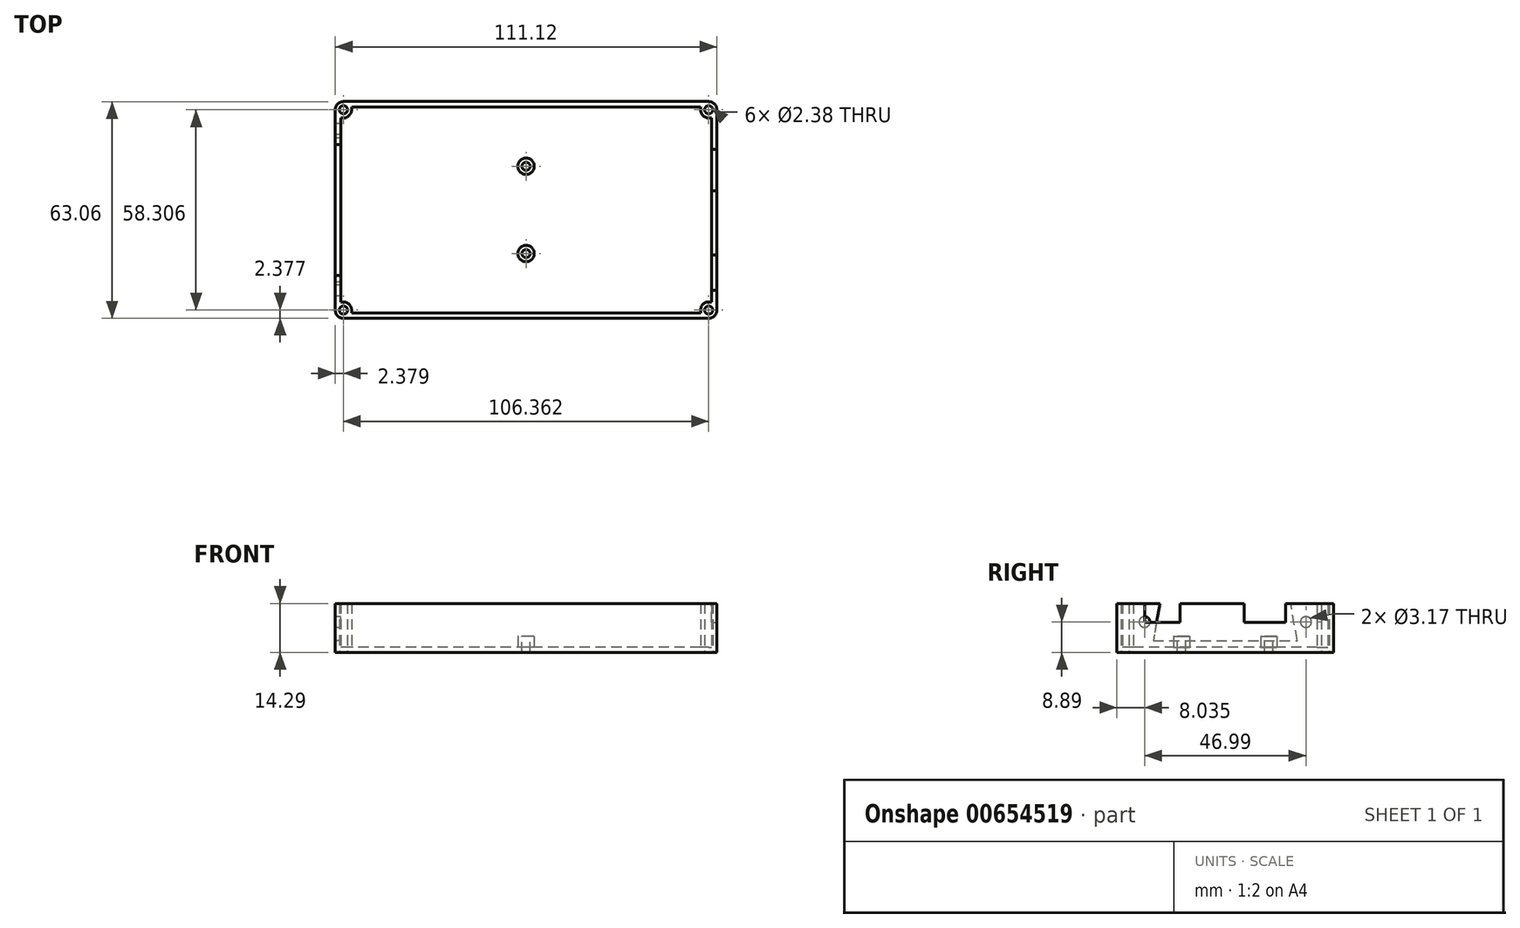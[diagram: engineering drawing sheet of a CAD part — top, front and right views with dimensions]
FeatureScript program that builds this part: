
annotation { "Feature Type Name" : "Feature", "Feature Type Description" : "" }
export const myFeature = defineFeature(function(context is Context, id is Id, definition is map)
    precondition{}
    {
        {
            var Q0;
            Q0=qCreatedBy(makeId("Top.planeOp"),FACE);
            var sketch = newSketch(context, id + "F0", { "sketchPlane" : qUnion([Q0])});
            skLineSegment(sketch, "E0.bottom", {"start": v(50.8, 26.77) * mm, "end": v(-50.8, 26.77) * mm});
            skLineSegment(sketch, "E0.top", {"start": v(50.8, -26.77) * mm, "end": v(-50.8, -26.77) * mm});
            skLineSegment(sketch, "E0.left", {"start": v(50.8, 26.77) * mm, "end": v(50.8, -26.77) * mm});
            skLineSegment(sketch, "E0.right", {"start": v(-50.8, 26.77) * mm, "end": v(-50.8, -26.77) * mm});
            skPoint(sketch, "E0.middle", {"position": v(0, 0) * mm});
            skSolve(sketch);
        }
        {
            var Q0;
            Q0=qCreatedBy(makeId("Top.planeOp"),FACE);
            var sketch = newSketch(context, id + "F1", { "sketchPlane" : qUnion([Q0])});
            skLineSegment(sketch, "E1.bottom", {"start": v(55.56, 31.53) * mm, "end": v(-55.56, 31.53) * mm});
            skLineSegment(sketch, "E1.top", {"start": v(55.56, -31.53) * mm, "end": v(-55.56, -31.53) * mm});
            skLineSegment(sketch, "E1.left", {"start": v(55.56, 31.53) * mm, "end": v(55.56, -31.53) * mm});
            skLineSegment(sketch, "E1.right", {"start": v(-55.56, 31.53) * mm, "end": v(-55.56, -31.53) * mm});
            skPoint(sketch, "E1.middle", {"position": v(0, 0) * mm});
            skLineSegment(sketch, "E2.bottom", {"start": v(53.97, 29.95) * mm, "end": v(-53.98, 29.95) * mm, "construction": true});
            skLineSegment(sketch, "E2.top", {"start": v(53.98, -29.95) * mm, "end": v(-53.97, -29.95) * mm, "construction": true});
            skLineSegment(sketch, "E2.left", {"start": v(53.97, 29.95) * mm, "end": v(53.98, -29.95) * mm, "construction": true});
            skLineSegment(sketch, "E2.right", {"start": v(-53.98, 29.95) * mm, "end": v(-53.97, -29.95) * mm, "construction": true});
            skSolve(sketch);
        }
        {
            var Q0;
            Q0=makeQuery(id+"F1.imprint","IMPRINT",FACE,{"disambiguationData":[TD([[makeQuery(id+"F1.imprint","IMPRINT",EDGE,{"derivedFrom":sQuery(id+"F1.wireOp",EDGE,"E1.bottom")}),1.0]])]});
            extrude(context, id + "F2", {"entities" : qUnion([Q0]), "depth" : 1.59 * mm, "offsetDistance" : 25.4 * mm});
        }
        {
            var Q0;
            Q0=makeQuery(id+"F2.opExtrude","CAP_FACE",FACE,{"disambiguationData":[OSD([sQuery(id+"F1.wireOp",EDGE,"E1.bottom"),sQuery(id+"F1.wireOp",EDGE,"E1.top"),sQuery(id+"F1.wireOp",EDGE,"E1.left"),sQuery(id+"F1.wireOp",EDGE,"E1.right")])],"isStart":false});
            var sketch = newSketch(context, id + "F3", { "sketchPlane" : qUnion([Q0])});
            skLineSegment(sketch, "E3.bottom", {"start": v(55.56, 31.53) * mm, "end": v(-55.56, 31.53) * mm});
            skLineSegment(sketch, "E3.top", {"start": v(55.56, -31.53) * mm, "end": v(-55.56, -31.53) * mm});
            skLineSegment(sketch, "E3.left", {"start": v(55.56, 31.53) * mm, "end": v(55.56, -31.53) * mm});
            skLineSegment(sketch, "E3.right", {"start": v(-55.56, 31.53) * mm, "end": v(-55.56, -31.53) * mm});
            skPoint(sketch, "E3.middle", {"position": v(0, 0) * mm});
            skLineSegment(sketch, "E4.left", {"start": v(53.97, 26.77) * mm, "end": v(53.97, -26.77) * mm});
            skLineSegment(sketch, "E4.right", {"start": v(-53.97, 26.77) * mm, "end": v(-53.97, -26.77) * mm});
            skArc(sketch, "E5", {"start": v(-53.18, 26.77) * mm, "mid": v(-51.5, 27.47) * mm, "end": v(-50.8, 29.15) * mm});
            skCircle(sketch, "E6", {"center": v(-53.18, 29.15) * mm, "radius": 1.2 * mm});
            skLineSegment(sketch, "E7", {"start": v(-50.8, 29.15) * mm, "end": v(-50.8, 29.95) * mm});
            skLineSegment(sketch, "E8", {"start": v(-53.18, 26.77) * mm, "end": v(-53.97, 26.77) * mm});
            skLineSegment(sketch, "E9", {"start": v(-55.56, 31.53) * mm, "end": v(-51.5, 27.47) * mm, "construction": true});
            skPoint(sketch, "E10", {"position": v(-53.53, 29.5) * mm});
            skPoint(sketch, "E11.orphan", {"position": v(-53.97, 37.1) * mm});
            skCircle(sketch, "E12.MirrorC", {"center": v(-53.18, -29.15) * mm, "radius": 1.2 * mm});
            skLineSegment(sketch, "E13.MirrorCS", {"start": v(-53.18, -26.77) * mm, "end": v(-53.97, -26.77) * mm});
            skArc(sketch, "E14.MirrorCS", {"start": v(-53.18, -26.77) * mm, "mid": v(-51.5, -27.47) * mm, "end": v(-50.8, -29.15) * mm});
            skLineSegment(sketch, "E15.MirrorCS", {"start": v(-50.8, -29.15) * mm, "end": v(-50.8, -29.95) * mm});
            skCircle(sketch, "E16.MirrorC", {"center": v(53.18, 29.15) * mm, "radius": 1.2 * mm});
            skLineSegment(sketch, "E17.MirrorCS", {"start": v(50.8, 29.15) * mm, "end": v(50.8, 29.95) * mm});
            skArc(sketch, "E18.MirrorCS", {"start": v(53.18, 26.77) * mm, "mid": v(51.5, 27.47) * mm, "end": v(50.8, 29.15) * mm});
            skLineSegment(sketch, "E19.MirrorCS", {"start": v(53.18, 26.77) * mm, "end": v(53.97, 26.77) * mm});
            skCircle(sketch, "E20.MirrorC", {"center": v(53.18, -29.15) * mm, "radius": 1.2 * mm});
            skLineSegment(sketch, "E21.MirrorCS", {"start": v(53.18, -26.77) * mm, "end": v(53.97, -26.77) * mm});
            skArc(sketch, "E22.MirrorCS", {"start": v(53.18, -26.77) * mm, "mid": v(51.5, -27.47) * mm, "end": v(50.8, -29.15) * mm});
            skLineSegment(sketch, "E23.MirrorCS", {"start": v(50.8, -29.15) * mm, "end": v(50.8, -29.95) * mm});
            skPoint(sketch, "E24.orphan", {"position": v(-53.97, -36.92) * mm});
            skLineSegment(sketch, "E25.trimOffspring", {"start": v(50.8, -29.95) * mm, "end": v(-50.8, -29.95) * mm});
            skPoint(sketch, "E26.orphan", {"position": v(53.97, -37.1) * mm});
            skLineSegment(sketch, "E27.trimOffspring", {"start": v(50.8, 29.95) * mm, "end": v(-50.8, 29.95) * mm});
            skPoint(sketch, "E28.orphan", {"position": v(53.97, 36.92) * mm});
            skSolve(sketch);
        }
        {
            var Q0;
            Q0=qSketchRegion(id+"F3",true);
            extrude(context, id + "F4", {"entities" : qUnion([Q0]), "operationType" : NewBodyOperationType.ADD, "depth" : 12.7 * mm, "offsetDistance" : 25.4 * mm});
        }
        {
            var Q0;
            Q0=makeQuery(id+"F4.boolean.opBoolean","MERGE",EDGE,{"derivedFrom":[makeQuery(id+"F2.opExtrude","SWEPT_EDGE",EDGE,{"disambiguationData":[OSD([sQuery(id+"F1.wireOp",EDGE,"E1.top"),sQuery(id+"F1.wireOp",EDGE,"E1.left")])]}),makeQuery(id+"F4.opExtrude","SWEPT_EDGE",EDGE,{"disambiguationData":[OSD([sQuery(id+"F3.wireOp",EDGE,"E3.top"),sQuery(id+"F3.wireOp",EDGE,"E3.left")])]})]});
            var Q1;
            Q1=makeQuery(id+"F4.boolean.opBoolean","MERGE",EDGE,{"derivedFrom":[makeQuery(id+"F2.opExtrude","SWEPT_EDGE",EDGE,{"disambiguationData":[OSD([sQuery(id+"F1.wireOp",EDGE,"E1.bottom"),sQuery(id+"F1.wireOp",EDGE,"E1.left")])]}),makeQuery(id+"F4.opExtrude","SWEPT_EDGE",EDGE,{"disambiguationData":[OSD([sQuery(id+"F3.wireOp",EDGE,"E3.bottom"),sQuery(id+"F3.wireOp",EDGE,"E3.left")])]})]});
            var Q2;
            Q2=makeQuery(id+"F4.boolean.opBoolean","MERGE",EDGE,{"derivedFrom":[makeQuery(id+"F2.opExtrude","SWEPT_EDGE",EDGE,{"disambiguationData":[OSD([sQuery(id+"F1.wireOp",EDGE,"E1.top"),sQuery(id+"F1.wireOp",EDGE,"E1.right")])]}),makeQuery(id+"F4.opExtrude","SWEPT_EDGE",EDGE,{"disambiguationData":[OSD([sQuery(id+"F3.wireOp",EDGE,"E3.top"),sQuery(id+"F3.wireOp",EDGE,"E3.right")])]})]});
            var Q3;
            Q3=makeQuery(id+"F4.boolean.opBoolean","MERGE",EDGE,{"derivedFrom":[makeQuery(id+"F2.opExtrude","SWEPT_EDGE",EDGE,{"disambiguationData":[OSD([sQuery(id+"F1.wireOp",EDGE,"E1.bottom"),sQuery(id+"F1.wireOp",EDGE,"E1.right")])]}),makeQuery(id+"F4.opExtrude","SWEPT_EDGE",EDGE,{"disambiguationData":[OSD([sQuery(id+"F3.wireOp",EDGE,"E3.bottom"),sQuery(id+"F3.wireOp",EDGE,"E3.right")])]})]});
            fillet(context, id + "F5", {"entities" : qUnion([Q0, Q1, Q2, Q3]), "radius" : 2.38 * mm, "tangentPropagation" : true, "allowEdgeOverflow" : false});
        }
        {
            var Q0;
            Q0=makeQuery(id+"F4.boolean.opBoolean","MERGE",FACE,{"derivedFrom":[makeQuery(id+"F2.opExtrude","SWEPT_FACE",FACE,{"disambiguationData":[OSD([sQuery(id+"F1.wireOp",EDGE,"E1.left")])]}),makeQuery(id+"F4.opExtrude","SWEPT_FACE",FACE,{"disambiguationData":[OSD([sQuery(id+"F3.wireOp",EDGE,"E3.left")])]})]});
            var sketch = newSketch(context, id + "F6", { "sketchPlane" : qUnion([Q0])});
            skLineSegment(sketch, "E29.bottom", {"start": v(-17.59, 14.29) * mm, "end": v(-13.14, 14.29) * mm});
            skLineSegment(sketch, "E29.top", {"start": v(-17.59, 8.76) * mm, "end": v(-13.14, 8.76) * mm});
            skLineSegment(sketch, "E30.top", {"start": v(13.14, 8.76) * mm, "end": v(17.59, 8.76) * mm});
            skPoint(sketch, "E31", {"position": v(-11.56, 8.76) * mm});
            skPoint(sketch, "E32", {"position": v(18.29, 8.76) * mm});
            skLineSegment(sketch, "E33.MirrorCS", {"start": v(5.52, 14.29) * mm, "end": v(5.52, 8.76) * mm});
            skLineSegment(sketch, "E34.MirrorCS", {"start": v(13.14, 8.76) * mm, "end": v(5.52, 8.76) * mm});
            skLineSegment(sketch, "E35.MirrorCS", {"start": v(17.59, 14.29) * mm, "end": v(17.59, 8.76) * mm});
            skLineSegment(sketch, "E36.MirrorCS", {"start": v(-17.59, 14.29) * mm, "end": v(-23.43, 14.29) * mm});
            skLineSegment(sketch, "E37.MirrorCS", {"start": v(-17.59, 8.76) * mm, "end": v(-23.43, 8.76) * mm});
            skPoint(sketch, "E38.MirrorP", {"position": v(-18.29, 8.76) * mm});
            skLineSegment(sketch, "E39.MirrorCS", {"start": v(-13.14, 14.29) * mm, "end": v(-13.14, 8.76) * mm});
            skLineSegment(sketch, "E40.MirrorCS", {"start": v(-23.43, 14.29) * mm, "end": v(-23.43, 8.76) * mm});
            skLineSegment(sketch, "E41.MirrorCS", {"start": v(17.59, 14.29) * mm, "end": v(5.52, 14.29) * mm});
            skPoint(sketch, "E42.MirrorP", {"position": v(11.56, 8.76) * mm});
            skPoint(sketch, "E43.orphan", {"position": v(23.43, 14.29) * mm});
            skPoint(sketch, "E44.orphan", {"position": v(23.43, 8.76) * mm});
            skPoint(sketch, "E30.bottom.start.orphan", {"position": v(13.14, 14.29) * mm});
            skPoint(sketch, "E29.right.end.orphan", {"position": v(-5.52, 8.76) * mm});
            skPoint(sketch, "E45.orphan", {"position": v(-5.52, 14.29) * mm});
            skSolve(sketch);
        }
        {
            var Q0;
            Q0=qSketchRegion(id+"F6",true);
            extrude(context, id + "F7", {"entities" : qUnion([Q0]), "operationType" : NewBodyOperationType.REMOVE, "endBound" : BoundingType.UP_TO_NEXT, "oppositeDirection" : true, "depth" : 25.4 * mm, "offsetDistance" : 25.4 * mm});
        }
        {
            var Q0;
            Q0=makeQuery(id+"F0.imprint","IMPRINT",FACE,{"disambiguationData":[TD([[makeQuery(id+"F0.imprint","IMPRINT",EDGE,{"derivedFrom":sQuery(id+"F0.wireOp",EDGE,"E0.bottom")}),1.0]])]});
            var sketch = newSketch(context, id + "F8", { "sketchPlane" : qUnion([Q0])});
            skLineSegment(sketch, "E46.bottom", {"start": v(-42.55, -25.36) * mm, "end": v(33.02, -25.36) * mm});
            skLineSegment(sketch, "E46.top", {"start": v(-42.55, -22.18) * mm, "end": v(33.02, -22.18) * mm});
            skLineSegment(sketch, "E46.left", {"start": v(-42.55, -25.36) * mm, "end": v(-42.55, -22.18) * mm});
            skLineSegment(sketch, "E46.right", {"start": v(33.02, -25.36) * mm, "end": v(33.02, -22.18) * mm});
            skPoint(sketch, "E47", {"position": v(-42.55, -23.77) * mm});
            skLineSegment(sketch, "E48.MirrorCS", {"start": v(33.02, 25.36) * mm, "end": v(33.02, 22.18) * mm});
            skLineSegment(sketch, "E49.MirrorCS", {"start": v(-42.55, 25.36) * mm, "end": v(-42.55, 22.18) * mm});
            skLineSegment(sketch, "E50.MirrorCS", {"start": v(-42.55, 22.18) * mm, "end": v(33.02, 22.18) * mm});
            skLineSegment(sketch, "E51.MirrorCS", {"start": v(-42.55, 25.36) * mm, "end": v(33.02, 25.36) * mm});
            skPoint(sketch, "E52.MirrorP", {"position": v(-42.55, 23.77) * mm});
            skSolve(sketch);
        }
        {
            var Q0;
            Q0=makeQuery(id+"F4.boolean.opBoolean","MERGE",FACE,{"derivedFrom":[makeQuery(id+"F2.opExtrude","SWEPT_FACE",FACE,{"disambiguationData":[OSD([sQuery(id+"F1.wireOp",EDGE,"E1.right")])]}),makeQuery(id+"F4.opExtrude","SWEPT_FACE",FACE,{"disambiguationData":[OSD([sQuery(id+"F3.wireOp",EDGE,"E3.right")])]})]});
            var sketch = newSketch(context, id + "F9", { "sketchPlane" : qUnion([Q0])});
            skLineSegment(sketch, "E53", {"start": v(-19.05, 14.29) * mm, "end": v(19.05, 14.29) * mm});
            skLineSegment(sketch, "E54", {"start": v(19.05, 14.29) * mm, "end": v(20.95, 3.5) * mm});
            skLineSegment(sketch, "E55", {"start": v(20.95, 3.5) * mm, "end": v(-20.96, 3.5) * mm});
            skLineSegment(sketch, "E56", {"start": v(-20.96, 3.5) * mm, "end": v(-19.05, 14.29) * mm});
            skPoint(sketch, "E57", {"position": v(0, 14.29) * mm});
            skPoint(sketch, "E58", {"position": v(0, 3.5) * mm});
            skCircle(sketch, "E59", {"center": v(-23.5, 8.9) * mm, "radius": 1.59 * mm});
            skCircle(sketch, "E60", {"center": v(23.5, 8.9) * mm, "radius": 1.59 * mm});
            skLineSegment(sketch, "E61", {"start": v(0, 14.29) * mm, "end": v(0, 3.5) * mm, "construction": true});
            skPoint(sketch, "E62", {"position": v(0, 8.89) * mm});
            skSolve(sketch);
        }
        {
            var Q0;
            Q0 = qSketchRegion(id + "F9", true);
            extrude(context, id + "F10", {"entities" : qUnion([Q0]), "operationType" : NewBodyOperationType.REMOVE, "endBound" : BoundingType.UP_TO_NEXT, "oppositeDirection" : true, "depth" : 25.4 * mm, "offsetDistance" : 25.4 * mm});
        }
        {
            var Q0;
            Q0=makeQuery(id+"F4.boolean.opBoolean","SPLIT",FACE,{"disambiguationData":[TD([makeQuery(id+"F4.opExtrude","SWEPT_FACE",FACE,{"disambiguationData":[OSD([sQuery(id+"F3.wireOp",EDGE,"E4.left")])]})])],"derivedFrom":makeQuery(id+"F2.opExtrude","CAP_FACE",FACE,{"disambiguationData":[OSD([sQuery(id+"F1.wireOp",EDGE,"E1.bottom"),sQuery(id+"F1.wireOp",EDGE,"E1.top"),sQuery(id+"F1.wireOp",EDGE,"E1.left"),sQuery(id+"F1.wireOp",EDGE,"E1.right")])],"isStart":false})});
            var sketch = newSketch(context, id + "F11", { "sketchPlane" : qUnion([Q0])});
            skCircle(sketch, "E63", {"center": v(0, 12.7) * mm, "radius": 2.38 * mm});
            skCircle(sketch, "E64.MirrorC", {"center": v(0, -12.7) * mm, "radius": 2.38 * mm});
            skSolve(sketch);
        }
        {
            var Q0;
            Q0 = qSketchRegion(id + "F11", true);
            extrude(context, id + "F12", {"entities" : qUnion([Q0]), "operationType" : NewBodyOperationType.ADD, "depth" : 3.17 * mm, "offsetDistance" : 25.4 * mm});
        }
        {
            var Q0;
            Q0=makeQuery(id+"F12.opExtrude","CAP_FACE",FACE,{"disambiguationData":[OSD([sQuery(id+"F11.wireOp",EDGE,"E63")])],"isStart":false});
            var sketch = newSketch(context, id + "F13", { "sketchPlane" : qUnion([Q0])});
            skCircle(sketch, "E65", {"center": v(0, 12.7) * mm, "radius": 1.2 * mm});
            skCircle(sketch, "E66.MirrorC", {"center": v(0, -12.7) * mm, "radius": 1.2 * mm});
            skSolve(sketch);
        }
        {
            var Q0;
            Q0 = qSketchRegion(id + "F13", true);
            extrude(context, id + "F14", {"entities" : qUnion([Q0]), "operationType" : NewBodyOperationType.REMOVE, "endBound" : BoundingType.THROUGH_ALL, "oppositeDirection" : true, "depth" : 25.4 * mm, "offsetDistance" : 25.4 * mm});
        }
        {
            var Q0;
            {var subQ0=sQuery(id+"F3.wireOp",EDGE,"E6");var subQ2=sQuery(id+"F3.wireOp",EDGE,"E5");var subQ4=sQuery(id+"F3.wireOp",EDGE,"E4.right");var subQ6=sQuery(id+"F3.wireOp",EDGE,"E4.left");var subQ8=sQuery(id+"F3.wireOp",EDGE,"E3.right");var subQ10=sQuery(id+"F1.wireOp",EDGE,"E1.bottom");var subQ11=makeQuery(id+"F2.opExtrude","SWEPT_FACE",FACE,{"disambiguationData":[OSD([subQ10])]});var subQ12=sQuery(id+"F3.wireOp",EDGE,"E19.MirrorCS");var subQ14=sQuery(id+"F3.wireOp",EDGE,"E3.bottom");var subQ17=sQuery(id+"F3.wireOp",EDGE,"E3.left");var subQ23=sQuery(id+"F3.wireOp",EDGE,"E7");var subQ25=sQuery(id+"F3.wireOp",EDGE,"E8");var subQ28=sQuery(id+"F3.wireOp",EDGE,"E16.MirrorC");var subQ30=sQuery(id+"F3.wireOp",EDGE,"E17.MirrorCS");var subQ32=sQuery(id+"F3.wireOp",EDGE,"E18.MirrorCS");var subQ35=sQuery(id+"F3.wireOp",EDGE,"E27.trimOffspring");var subQ37=sQuery(id+"F3.wireOp",EDGE,"E15.MirrorCS");var subQ38=sQuery(id+"F3.wireOp",EDGE,"E14.MirrorCS");var subQ39=sQuery(id+"F3.wireOp",EDGE,"E13.MirrorCS");var subQ40=sQuery(id+"F3.wireOp",EDGE,"E12.MirrorC");var subQ41=sQuery(id+"F3.wireOp",EDGE,"E3.top");var subQ43=sQuery(id+"F3.wireOp",EDGE,"E22.MirrorCS");var subQ44=sQuery(id+"F3.wireOp",EDGE,"E25.trimOffspring");var subQ45=sQuery(id+"F3.wireOp",EDGE,"E23.MirrorCS");var subQ46=sQuery(id+"F3.wireOp",EDGE,"E20.MirrorC");var subQ47=sQuery(id+"F3.wireOp",EDGE,"E21.MirrorCS");Q0=makeQuery(id+"F10.boolean.opBoolean","SPLIT",FACE,{"disambiguationData":[TD([subQ11])],"derivedFrom":makeQuery(id+"F7.boolean.opBoolean","SPLIT",FACE,{"disambiguationData":[TD([subQ11])],"derivedFrom":makeQuery(id+"F4.opExtrude","CAP_FACE",FACE,{"disambiguationData":[OSD([subQ14,subQ41,subQ17,subQ8,subQ6,subQ4,subQ2,subQ0,subQ23,subQ25,subQ40,subQ39,subQ38,subQ37,subQ28,subQ30,subQ32,subQ12,subQ46,subQ47,subQ43,subQ45,subQ44,subQ35])],"isStart":false})})});}
            var sketch = newSketch(context, id + "F15", { "sketchPlane" : qUnion([Q0])});
            skCircle(sketch, "E67.0", {"center": v(53.18, 29.15) * mm, "radius": 1.2 * mm});
            skCircle(sketch, "E68.0", {"center": v(53.18, -29.15) * mm, "radius": 1.2 * mm});
            skCircle(sketch, "E69.0", {"center": v(-53.18, -29.15) * mm, "radius": 1.2 * mm});
            skCircle(sketch, "E70.0", {"center": v(-53.18, 29.15) * mm, "radius": 1.2 * mm});
            skSolve(sketch);
        }
        {
            var Q0;
            Q0 = qSketchRegion(id + "F15", true);
            extrude(context, id + "F16", {"entities" : qUnion([Q0]), "operationType" : NewBodyOperationType.REMOVE, "endBound" : BoundingType.THROUGH_ALL, "oppositeDirection" : true, "depth" : 25.4 * mm, "offsetDistance" : 25.4 * mm});
        }
    });
